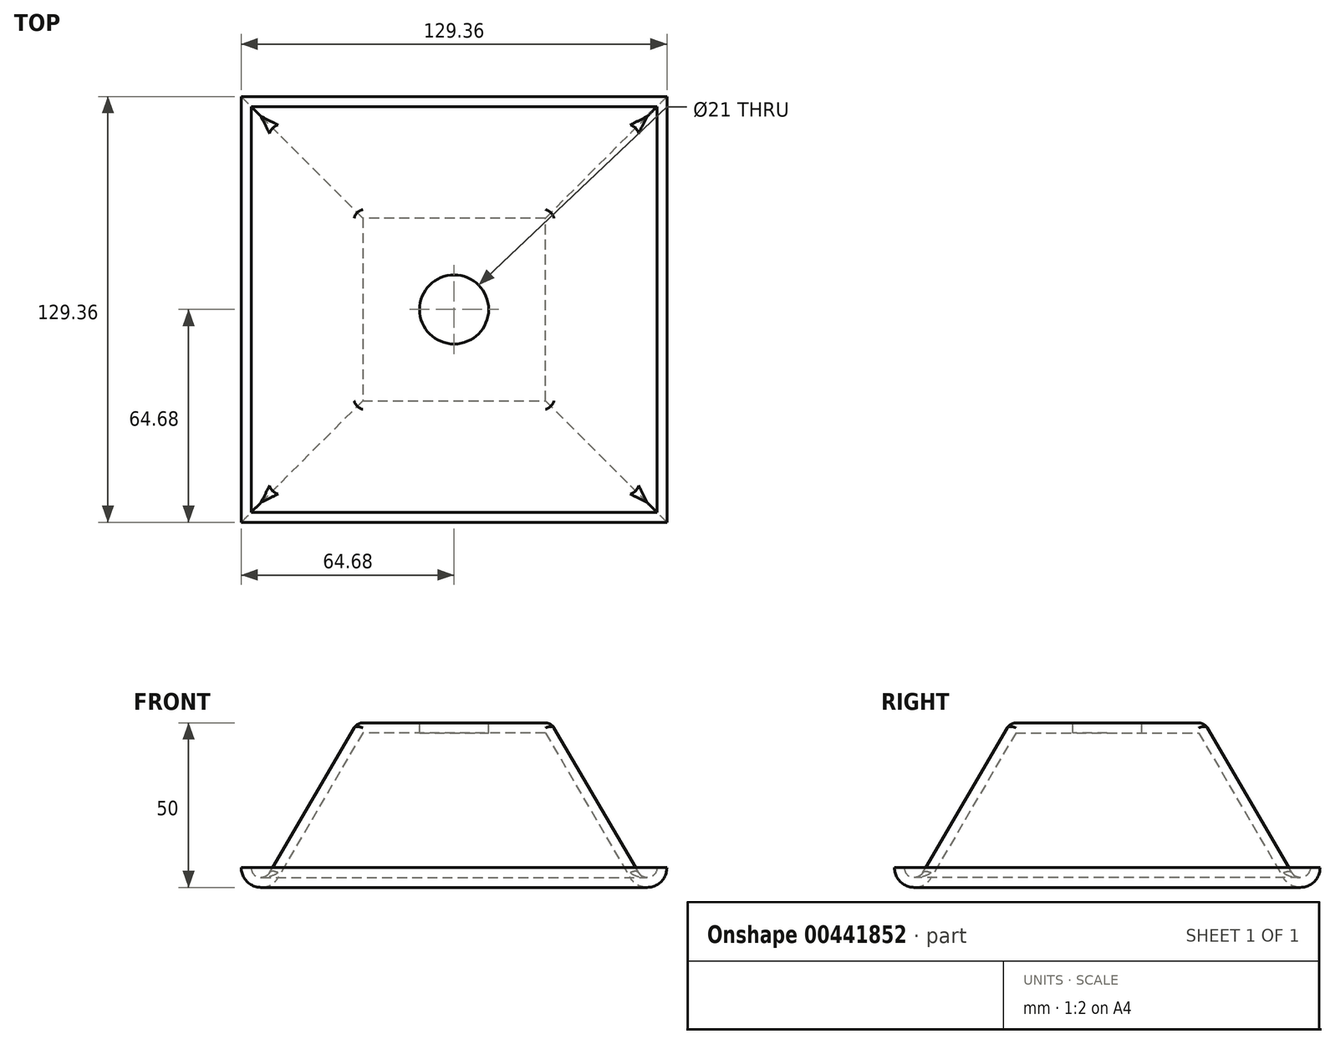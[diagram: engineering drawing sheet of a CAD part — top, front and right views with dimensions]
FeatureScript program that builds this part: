
annotation { "Feature Type Name" : "Feature", "Feature Type Description" : "" }
export const myFeature = defineFeature(function(context is Context, id is Id, definition is map)
    precondition{}
    {
        {
            var Q0;
            Q0=qCreatedBy(makeId("Front.planeOp"),FACE);
            var sketch = newSketch(context, id + "F0", { "sketchPlane" : qUnion([Q0])});
            skLineSegment(sketch, "E0", {"start": v(0, 0) * mm, "end": v(0, 69.3) * mm, "construction": true});
            skLineSegment(sketch, "E1.MirrorCS", {"start": v(0, 47.03) * mm, "end": v(-29.5, 47.03) * mm});
            skLineSegment(sketch, "E2.MirrorCS", {"start": v(-29.5, 47.03) * mm, "end": v(-56.1, 1.51) * mm});
            skLineSegment(sketch, "E3.0", {"start": v(-27.78, 44.03) * mm, "end": v(-53.5, 0) * mm});
            skLineSegment(sketch, "E4.0", {"start": v(0, 44.03) * mm, "end": v(-27.78, 44.03) * mm});
            skLineSegment(sketch, "E5", {"start": v(-53.5, 0) * mm, "end": v(-53.5, 0) * mm});
            skLineSegment(sketch, "E6", {"start": v(0, 47.03) * mm, "end": v(0, 44.03) * mm});
            skArc(sketch, "E7", {"start": v(-64.68, 3.03) * mm, "mid": v(-60.25, -2.76) * mm, "end": v(-53.5, 0) * mm});
            skLineSegment(sketch, "E8", {"start": v(-61.68, 3.03) * mm, "end": v(-64.68, 3.03) * mm});
            skArc(sketch, "E9.0", {"start": v(-61.68, 3.03) * mm, "mid": v(-59.3, 0.1) * mm, "end": v(-55.94, 1.8) * mm});
            skPoint(sketch, "E10.orphan", {"position": v(-56.97, 0) * mm});
            skSolve(sketch);
        }
        {
            var Q0;
            Q0=qCreatedBy(makeId("Top.planeOp"),FACE);
            var sketch = newSketch(context, id + "F1", { "sketchPlane" : qUnion([Q0])});
            skLineSegment(sketch, "E11.bottom", {"start": v(-65, 65) * mm, "end": v(65, 65) * mm});
            skLineSegment(sketch, "E11.top", {"start": v(-65, -65) * mm, "end": v(65, -65) * mm});
            skLineSegment(sketch, "E11.left", {"start": v(-65, 65) * mm, "end": v(-65, -65) * mm});
            skLineSegment(sketch, "E11.right", {"start": v(65, 65) * mm, "end": v(65, -65) * mm});
            skPoint(sketch, "E11.middle", {"position": v(0, 0) * mm});
            skSolve(sketch);
        }
        {
            var Q0;
            Q0=makeQuery(id+"F0.imprint","IMPRINT",FACE,{"disambiguationData":[TD([[makeQuery(id+"F0.imprint","IMPRINT",EDGE,{"derivedFrom":sQuery(id+"F0.wireOp",EDGE,"E1.MirrorCS")}),1.0]])]});
            var Q1;
            Q1=sQuery(id+"F1.wireOp",EDGE,"E11.left");
            var Q2;
            Q2=sQuery(id+"F1.wireOp",EDGE,"E11.bottom");
            var Q3;
            Q3=sQuery(id+"F1.wireOp",EDGE,"E11.right");
            var Q4;
            Q4=sQuery(id+"F1.wireOp",EDGE,"E11.top");
            sweep(context, id + "F2", {"profiles" : qUnion([Q0]), "path" : qUnion([Q1, Q2, Q3, Q4])});
        }
        {
            var Q0;
            Q0=makeQuery(id+"F2.opSweep","SWEPT_FACE",FACE,{"disambiguationData":[OSD([sQuery(id+"F0.wireOp",EDGE,"E1.MirrorCS"),sQuery(id+"F1.wireOp",EDGE,"E11.left")])]});
            var sketch = newSketch(context, id + "F3", { "sketchPlane" : qUnion([Q0])});
            skCircle(sketch, "E12", {"center": v(0, 0) * mm, "radius": 10.5 * mm});
            skSolve(sketch);
        }
        {
            var Q0;
            Q0=makeQuery(id+"F3.imprint","IMPRINT",FACE,{"disambiguationData":[TD([[makeQuery(id+"F3.imprint","IMPRINT",EDGE,{"derivedFrom":sQuery(id+"F3.wireOp",EDGE,"E12")}),1.0]])]});
            extrude(context, id + "F4", {"entities" : qUnion([Q0]), "operationType" : NewBodyOperationType.REMOVE, "oppositeDirection" : true, "depth" : 25 * mm});
        }
        {
            var Q0;
            Q0=makeQuery(id+"F2.opSweep","SWEPT_EDGE",EDGE,{"disambiguationData":[OSD([sQuery(id+"F0.wireOp",EDGE,"E1.MirrorCS"),sQuery(id+"F0.wireOp",EDGE,"E2.MirrorCS"),sQuery(id+"F1.wireOp",EDGE,"E11.right")])]});
            var Q1;
            Q1=makeQuery(id+"F2.opSweep","SWEPT_EDGE",EDGE,{"disambiguationData":[OSD([sQuery(id+"F0.wireOp",EDGE,"E1.MirrorCS"),sQuery(id+"F0.wireOp",EDGE,"E2.MirrorCS"),sQuery(id+"F1.wireOp",EDGE,"E11.bottom")])]});
            var Q2;
            Q2=makeQuery(id+"F2.opSweep","SWEPT_EDGE",EDGE,{"disambiguationData":[OSD([sQuery(id+"F0.wireOp",EDGE,"E1.MirrorCS"),sQuery(id+"F0.wireOp",EDGE,"E2.MirrorCS"),sQuery(id+"F1.wireOp",EDGE,"E11.left")])]});
            var Q3;
            Q3=makeQuery(id+"F2.opSweep","SWEPT_EDGE",EDGE,{"disambiguationData":[OSD([sQuery(id+"F0.wireOp",EDGE,"E1.MirrorCS"),sQuery(id+"F0.wireOp",EDGE,"E2.MirrorCS"),sQuery(id+"F1.wireOp",EDGE,"E11.top")])]});
            var Q4;
            Q4=makeQuery(id+"F2.opSweep","MID_CAP_EDGE",EDGE,{"disambiguationData":[OSD([sQuery(id+"F0.wireOp",EDGE,"E2.MirrorCS"),sQuery(id+"F1.wireOp",VERTEX,"E11.right.start")])],"capPos":2.0});
            var Q5;
            Q5=makeQuery(id+"F2.opSweep","MID_CAP_EDGE",EDGE,{"disambiguationData":[OSD([sQuery(id+"F0.wireOp",EDGE,"E2.MirrorCS"),sQuery(id+"F1.wireOp",VERTEX,"E11.bottom.start")])],"capPos":1.0});
            var Q6;
            Q6=makeQuery(id+"F2.opSweep","MID_CAP_EDGE",EDGE,{"disambiguationData":[OSD([sQuery(id+"F0.wireOp",EDGE,"E2.MirrorCS"),sQuery(id+"F1.wireOp",VERTEX,"E11.top.end")])],"capPos":3.0});
            var Q7;
            Q7=makeQuery(id+"F2.opSweep","CAP_EDGE",EDGE,{"disambiguationData":[OSD([sQuery(id+"F0.wireOp",EDGE,"E2.MirrorCS"),sQuery(id+"F1.wireOp",VERTEX,"E11.top.start")])],"isStart":true});
            fillet(context, id + "F5", {"entities" : qUnion([Q0, Q1, Q2, Q3, Q4, Q5, Q6, Q7]), "radius" : 3 * mm, "tangentPropagation" : true, "allowEdgeOverflow" : false});
        }
    });
